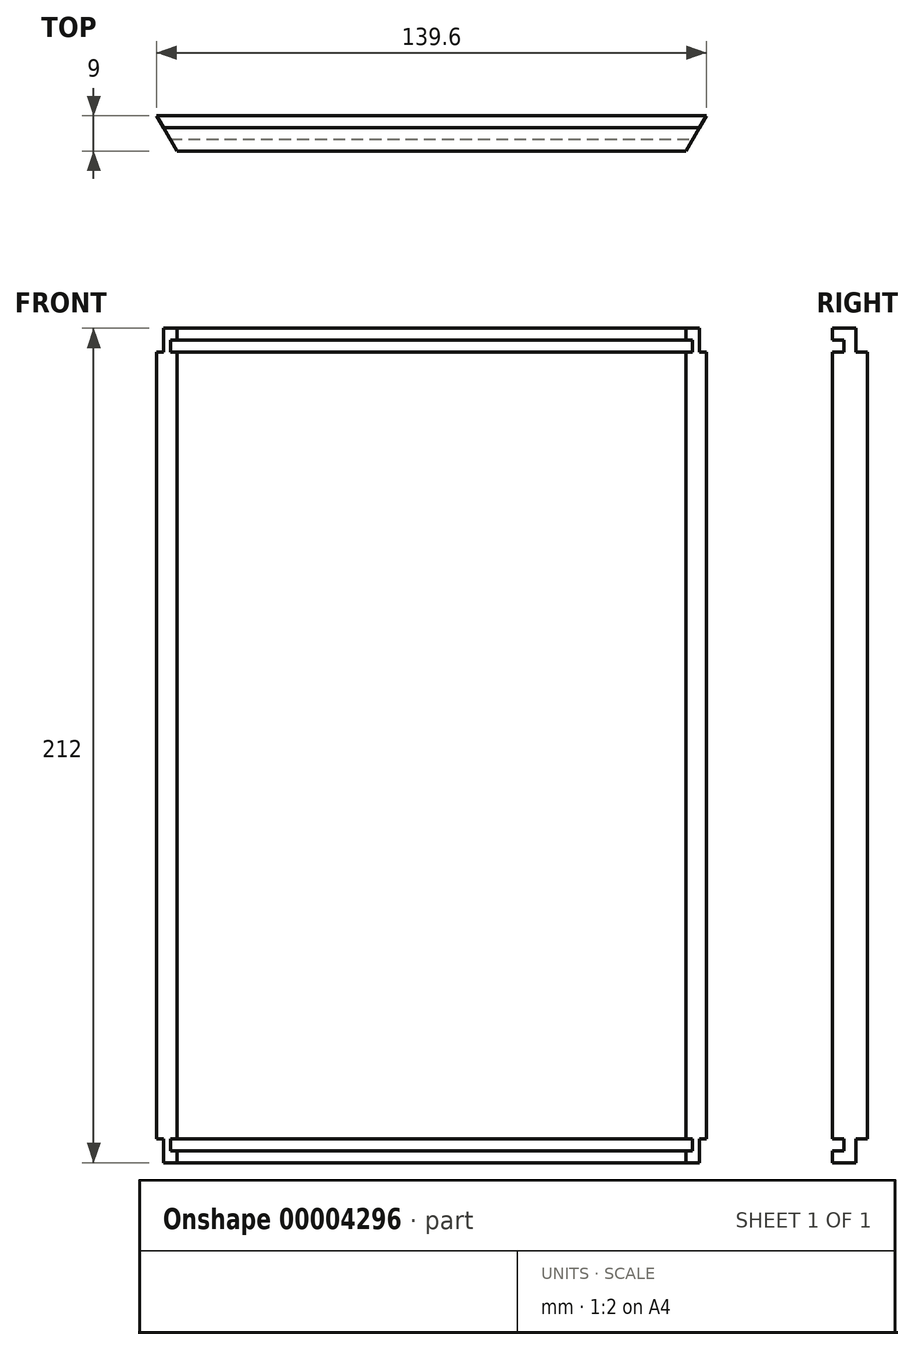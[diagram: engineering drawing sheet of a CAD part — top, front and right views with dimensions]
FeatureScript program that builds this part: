
annotation { "Feature Type Name" : "Feature", "Feature Type Description" : "" }
export const myFeature = defineFeature(function(context is Context, id is Id, definition is map)
    precondition{}
    {
        {
            var Q0;
            Q0=qCreatedBy(makeId("Front.planeOp"),FACE);
            var sketch = newSketch(context, id + "F0", { "sketchPlane" : qUnion([Q0])});
            skLineSegment(sketch, "E0.bottom", {"start": v(-52.97, 148.92) * mm, "end": v(97.03, 148.92) * mm});
            skLineSegment(sketch, "E0.top", {"start": v(-52.97, -51.08) * mm, "end": v(97.03, -51.08) * mm});
            skLineSegment(sketch, "E0.left", {"start": v(-52.97, 148.92) * mm, "end": v(-52.97, -51.08) * mm});
            skLineSegment(sketch, "E0.right", {"start": v(97.03, 148.92) * mm, "end": v(97.03, -51.08) * mm});
            skSolve(sketch);
        }
        {
            var Q0;
            Q0=makeQuery(id+"F0.imprint","IMPRINT",FACE,{"disambiguationData":[TD([[makeQuery(id+"F0.imprint","IMPRINT",EDGE,{"derivedFrom":sQuery(id+"F0.wireOp",EDGE,"E0.bottom")}),-1.0]])]});
            extrude(context, id + "F1", {"entities" : qUnion([Q0]), "depth" : 9 * mm});
        }
        {
            var Q0;
            Q0=makeQuery(id+"F1.opExtrude","SWEPT_FACE",FACE,{"disambiguationData":[OSD([sQuery(id+"F0.wireOp",EDGE,"E0.bottom")])]});
            var sketch = newSketch(context, id + "F2", { "sketchPlane" : qUnion([Q0])});
            skLineSegment(sketch, "E1", {"start": v(-52.97, 0) * mm, "end": v(-52.97, -9) * mm});
            skLineSegment(sketch, "E2", {"start": v(-52.97, -9) * mm, "end": v(97.03, -9) * mm});
            skLineSegment(sketch, "E3", {"start": v(97.03, -9) * mm, "end": v(97.03, 0) * mm});
            skLineSegment(sketch, "E4", {"start": v(97.03, 0) * mm, "end": v(-52.97, 0) * mm});
            skLineSegment(sketch, "E5.0", {"start": v(91.83, -9) * mm, "end": v(91.83, 0) * mm});
            skLineSegment(sketch, "E6", {"start": v(97.03, 0) * mm, "end": v(91.83, -9) * mm});
            skLineSegment(sketch, "E7.0", {"start": v(-46.04, 0) * mm, "end": v(-46.04, -9) * mm});
            skLineSegment(sketch, "E8.0", {"start": v(-40.84, 0) * mm, "end": v(-40.84, -9) * mm});
            skLineSegment(sketch, "E9", {"start": v(-40.84, -9) * mm, "end": v(-46.04, 0) * mm});
            skSolve(sketch);
        }
        {
            var Q0;
            Q0=makeQuery(id+"F1.opExtrude","SWEPT_FACE",FACE,{"disambiguationData":[OSD([sQuery(id+"F0.wireOp",EDGE,"E0.top")])]});
            var sketch = newSketch(context, id + "F3", { "sketchPlane" : qUnion([Q0])});
            skLineSegment(sketch, "E10.0", {"start": v(-52.97, 6) * mm, "end": v(97.03, 6) * mm});
            skLineSegment(sketch, "E11.0", {"start": v(-52.97, 3) * mm, "end": v(97.03, 3) * mm});
            skSolve(sketch);
        }
        {
            var Q0;
            {var subQ3=sQuery(id+"F3.wireOp",EDGE,"E10.0");Q0=makeQuery(id+"F3.imprint","IMPRINT",FACE,{"disambiguationData":[TD([[makeQuery(id+"F3.imprint","IMPRINT",EDGE,{"derivedFrom":subQ3}),-1.0]])]});}
            extrude(context, id + "F4", {"entities" : qUnion([Q0]), "operationType" : NewBodyOperationType.ADD, "depth" : 6 * mm});
        }
        {
            var Q0;
            Q0=makeQuery(id+"F4.opExtrude","SWEPT_FACE",FACE,{"disambiguationData":[OSD([sQuery(id+"F3.wireOp",EDGE,"E10.0")])]});
            var sketch = newSketch(context, id + "F5", { "sketchPlane" : qUnion([Q0])});
            skLineSegment(sketch, "E12.0", {"start": v(-52.97, -54.08) * mm, "end": v(97.03, -54.08) * mm});
            skSolve(sketch);
        }
        {
            var Q0;
            {var subQ3=sQuery(id+"F5.wireOp",EDGE,"E12.0");Q0=makeQuery(id+"F5.imprint","IMPRINT",FACE,{"disambiguationData":[TD([[makeQuery(id+"F5.imprint","IMPRINT",EDGE,{"derivedFrom":subQ3}),-1.0]])]});}
            extrude(context, id + "F6", {"entities" : qUnion([Q0]), "operationType" : NewBodyOperationType.ADD, "depth" : 3 * mm});
        }
        {
            var Q0;
            {var subQ2=sQuery(id+"F2.wireOp",EDGE,"E1");Q0=makeQuery(id+"F2.imprint","IMPRINT",FACE,{"disambiguationData":[TD([[makeQuery(id+"F2.imprint","IMPRINT",EDGE,{"derivedFrom":subQ2}),-1.0]])]});}
            var Q1;
            {var subQ1=sQuery(id+"F2.wireOp",EDGE,"E7.0");Q1=makeQuery(id+"F2.imprint","IMPRINT",FACE,{"disambiguationData":[TD([[makeQuery(id+"F2.imprint","IMPRINT",EDGE,{"derivedFrom":subQ1}),1.0]])]});}
            var Q2;
            {var subQ1=sQuery(id+"F2.wireOp",EDGE,"E3");Q2=makeQuery(id+"F2.imprint","IMPRINT",FACE,{"disambiguationData":[TD([[makeQuery(id+"F2.imprint","IMPRINT",EDGE,{"derivedFrom":subQ1}),1.0]])]});}
            extrude(context, id + "F7", {"entities" : qUnion([Q0, Q1, Q2]), "operationType" : NewBodyOperationType.REMOVE, "oppositeDirection" : true, "depth" : 228.53 * mm});
        }
        {
            var Q0;
            {var subQ0=sQuery(id+"F3.wireOp",EDGE,"E10.0");Q0=makeQuery(id+"F6.boolean.opBoolean","MERGE",FACE,{"derivedFrom":[makeQuery(id+"F4.opExtrude","CAP_FACE",FACE,{"disambiguationData":[OSD([sQuery(id+"F0.wireOp",EDGE,"E0.top"),sQuery(id+"F0.wireOp",EDGE,"E0.left"),sQuery(id+"F0.wireOp",EDGE,"E0.right"),subQ0,sQuery(id+"F3.wireOp",EDGE,"E11.0")])],"isStart":false}),makeQuery(id+"F6.opExtrude","SWEPT_FACE",FACE,{"disambiguationData":[OSD([subQ0])]})]});}
            var sketch = newSketch(context, id + "F8", { "sketchPlane" : qUnion([Q0])});
            skLineSegment(sketch, "E13.0", {"start": v(88.36, 9) * mm, "end": v(91.83, 3) * mm});
            skLineSegment(sketch, "E14", {"start": v(91.83, 9) * mm, "end": v(88.36, 9) * mm});
            skLineSegment(sketch, "E15", {"start": v(95.3, 3) * mm, "end": v(91.83, 3) * mm});
            skLineSegment(sketch, "E16", {"start": v(95.3, 3) * mm, "end": v(91.83, 9) * mm});
            skSolve(sketch);
        }
        {
            var Q0;
            Q0=makeQuery(id+"F8.imprint","IMPRINT",FACE,{"disambiguationData":[TD([[makeQuery(id+"F8.imprint","IMPRINT",EDGE,{"derivedFrom":sQuery(id+"F8.wireOp",EDGE,"E13.0")}),1.0]])]});
            extrude(context, id + "F9", {"entities" : qUnion([Q0]), "operationType" : NewBodyOperationType.REMOVE, "oppositeDirection" : true, "depth" : 3 * mm});
        }
        {
            var Q0;
            Q0=makeQuery(id+"F1.opExtrude","SWEPT_FACE",FACE,{"disambiguationData":[OSD([sQuery(id+"F0.wireOp",EDGE,"E0.bottom")])]});
            var sketch = newSketch(context, id + "F10", { "sketchPlane" : qUnion([Q0])});
            skLineSegment(sketch, "E17.0", {"start": v(-44.3, -3) * mm, "end": v(95.3, -3) * mm});
            skLineSegment(sketch, "E18.0", {"start": v(-42.58, -6) * mm, "end": v(93.56, -6) * mm});
            skLineSegment(sketch, "E19", {"start": v(-46.04, 0) * mm, "end": v(-40.84, -9) * mm});
            skLineSegment(sketch, "E20", {"start": v(97.03, 0) * mm, "end": v(91.83, -9) * mm});
            skSolve(sketch);
        }
        {
            var Q0;
            {var subQ2=sQuery(id+"F10.wireOp",EDGE,"E17.0");Q0=makeQuery(id+"F10.imprint","IMPRINT",FACE,{"disambiguationData":[TD([[makeQuery(id+"F10.imprint","IMPRINT",EDGE,{"derivedFrom":subQ2}),-1.0]])]});}
            extrude(context, id + "F11", {"entities" : qUnion([Q0]), "operationType" : NewBodyOperationType.ADD, "depth" : 6 * mm});
        }
        {
            var Q0;
            Q0=makeQuery(id+"F11.opExtrude","SWEPT_FACE",FACE,{"disambiguationData":[OSD([sQuery(id+"F10.wireOp",EDGE,"E18.0")])]});
            var sketch = newSketch(context, id + "F12", { "sketchPlane" : qUnion([Q0])});
            skLineSegment(sketch, "E21.0", {"start": v(-42.58, 151.92) * mm, "end": v(93.56, 151.92) * mm});
            skSolve(sketch);
        }
        {
            var Q0;
            {var subQ2=sQuery(id+"F12.wireOp",EDGE,"E21.0");Q0=makeQuery(id+"F12.imprint","IMPRINT",FACE,{"disambiguationData":[TD([[makeQuery(id+"F12.imprint","IMPRINT",EDGE,{"derivedFrom":subQ2}),1.0]])]});}
            extrude(context, id + "F13", {"entities" : qUnion([Q0]), "operationType" : NewBodyOperationType.ADD, "depth" : 3 * mm});
        }
        {
            var Q0;
            {var subQ0=sQuery(id+"F10.wireOp",EDGE,"E18.0");Q0=makeQuery(id+"F13.boolean.opBoolean","MERGE",FACE,{"derivedFrom":[makeQuery(id+"F11.opExtrude","CAP_FACE",FACE,{"disambiguationData":[OSD([sQuery(id+"F10.wireOp",EDGE,"E17.0"),subQ0,sQuery(id+"F10.wireOp",EDGE,"E19"),sQuery(id+"F10.wireOp",EDGE,"E20")])],"isStart":false}),makeQuery(id+"F13.opExtrude","SWEPT_FACE",FACE,{"disambiguationData":[OSD([subQ0])]})]});}
            var sketch = newSketch(context, id + "F14", { "sketchPlane" : qUnion([Q0])});
            skLineSegment(sketch, "E22", {"start": v(-44.3, -3) * mm, "end": v(-40.84, -9) * mm});
            skLineSegment(sketch, "E23", {"start": v(-42.58, -9) * mm, "end": v(93.56, -9) * mm});
            skLineSegment(sketch, "E24", {"start": v(93.56, -9) * mm, "end": v(93.56, -6) * mm});
            skLineSegment(sketch, "E25", {"start": v(91.83, -9) * mm, "end": v(95.3, -3) * mm});
            skSolve(sketch);
        }
        {
            var Q0;
            {var subQ1=makeQuery(id+"F13.opExtrude","SWEPT_EDGE",EDGE,{"disambiguationData":[OSD([sQuery(id+"F10.wireOp",EDGE,"E18.0"),sQuery(id+"F10.wireOp",EDGE,"E19")])]});Q0=makeQuery(id+"F14.imprint","IMPRINT",FACE,{"disambiguationData":[TD([[makeQuery(id+"F14.imprint","IMPRINT",EDGE,{"derivedFrom":subQ1}),-1.0]])]});}
            var Q1;
            {var subQ3=sQuery(id+"F14.wireOp",EDGE,"E24");Q1=makeQuery(id+"F14.imprint","IMPRINT",FACE,{"disambiguationData":[TD([[makeQuery(id+"F14.imprint","IMPRINT",EDGE,{"derivedFrom":subQ3}),1.0]])]});}
            extrude(context, id + "F15", {"entities" : qUnion([Q0, Q1]), "operationType" : NewBodyOperationType.REMOVE, "oppositeDirection" : true, "depth" : 3.35 * mm});
        }
        {
            var Q0;
            {var subQ0=sQuery(id+"F10.wireOp",EDGE,"E18.0");Q0=makeQuery(id+"F13.boolean.opBoolean","MERGE",FACE,{"derivedFrom":[makeQuery(id+"F11.opExtrude","CAP_FACE",FACE,{"disambiguationData":[OSD([sQuery(id+"F10.wireOp",EDGE,"E17.0"),subQ0,sQuery(id+"F10.wireOp",EDGE,"E19"),sQuery(id+"F10.wireOp",EDGE,"E20")])],"isStart":false}),makeQuery(id+"F13.opExtrude","SWEPT_FACE",FACE,{"disambiguationData":[OSD([subQ0])]})]});}
            var sketch = newSketch(context, id + "F16", { "sketchPlane" : qUnion([Q0])});
            skLineSegment(sketch, "E26", {"start": v(95.3, -3) * mm, "end": v(91.83, -9) * mm});
            skLineSegment(sketch, "E27", {"start": v(91.83, -9) * mm, "end": v(88.36, -9) * mm});
            skLineSegment(sketch, "E28", {"start": v(95.3, -3) * mm, "end": v(91.83, -3) * mm});
            skLineSegment(sketch, "E29.0", {"start": v(91.83, -3) * mm, "end": v(88.36, -9) * mm});
            skSolve(sketch);
        }
        {
            var Q0;
            Q0=makeQuery(id+"F16.imprint","IMPRINT",FACE,{"disambiguationData":[TD([[makeQuery(id+"F16.imprint","IMPRINT",EDGE,{"derivedFrom":sQuery(id+"F16.wireOp",EDGE,"E26")}),-1.0]])]});
            extrude(context, id + "F17", {"entities" : qUnion([Q0]), "operationType" : NewBodyOperationType.REMOVE, "oppositeDirection" : true, "depth" : 227.72 * mm});
        }
        {
            var Q0;
            {var subQ0=sQuery(id+"F0.wireOp",EDGE,"E0.bottom");Q0=makeQuery(id+"F11.boolean.opBoolean","SPLIT",FACE,{"disambiguationData":[TD([makeQuery(id+"F11.opExtrude","SWEPT_FACE",FACE,{"disambiguationData":[OSD([sQuery(id+"F10.wireOp",EDGE,"E17.0")])]})])],"derivedFrom":makeQuery(id+"F1.opExtrude","SWEPT_FACE",FACE,{"disambiguationData":[OSD([subQ0])]})});}
            var sketch = newSketch(context, id + "F18", { "sketchPlane" : qUnion([Q0])});
            skLineSegment(sketch, "E30.0", {"start": v(93.56, 0) * mm, "end": v(91.83, -3) * mm});
            skLineSegment(sketch, "E31", {"start": v(95.3, -3) * mm, "end": v(91.21, -3) * mm});
            skLineSegment(sketch, "E32", {"start": v(97.03, 0) * mm, "end": v(91.66, 0) * mm});
            skSolve(sketch);
        }
        {
            var Q0;
            {var subQ7=sQuery(id+"F18.wireOp",EDGE,"E30.0");Q0=makeQuery(id+"F18.imprint","IMPRINT",FACE,{"disambiguationData":[TD([[makeQuery(id+"F18.imprint","IMPRINT",EDGE,{"derivedFrom":subQ7}),1.0]])]});}
            extrude(context, id + "F19", {"entities" : qUnion([Q0]), "operationType" : NewBodyOperationType.REMOVE, "oppositeDirection" : true, "depth" : 207.46 * mm});
        }
    });
